# Revit family: CRTW1X4
name_source: partatom
category: Lighting Fixtures
units: mm (PartAtom-declared; Revit-internal decimal feet)

## family parameters
Always vertical = Yes
Cut with Voids When Loaded = No
Host = Ceiling
Light Source = Yes
Maintain Annotation Orientation = No
OmniClass Number = 23.80.70.11
OmniClass Title = Luminaries for Internal Lighting
Part Type = Normal
Room Calculation Point = No
Round Connector Dimension = Use Diameter
Shared = No

## types (5) — shared parameters
Color Filter = 16777215
Default Elevation = 0' - 0"
Description = LED Recessed Cleanroom Top Access Walkable with Overlapping Door Frame
Dimming Lamp Color Temperature Shift = <None>
Emit Shape Visible in Rendering = No
Emit from Rectangle Length = 1' - 3 3/32"
Emit from Rectangle Width = 4' - 3 3/32"
Housing Finish = <By Category>
Lamp = LED
Length = 4' - 3 3/32"
Lens Finish = <By Category>
Manufacturer = Certolux
Model = CRTW
Tilt Angle = 90.00°
URL = https://www.viscor.com
Voltage = 120 V
Width = 1' - 3 3/32"

## per-type parameters (varying)
| type | Apparent Load | Lamp Wattage | Photometric Web File |
| CRTAo1X4-LED840K035LUNV-DSA | 28 VA | 28 VA | CRTAO-1X4-LED840K035LUNV-DSA.ies |
| CRTAo1X4-LED840K055LUNV-DSA | 41 VA | 41 VA | CRTAO-1X4-LED840K055LUNV-DSA.ies |
| CRTAo1X4-LED840K070LUNV-DSA | 52 VA | 52 VA | CRTAO-1X4-LED840K070LUNV-DSA.ies |
| CRTAo1X4-LED840K100LUNV-DSA | 75 VA | 75 VA | CRTAO-1X4-LED840K100LUNV-DSA.ies |
| CRTAo1X4-LED840K120LUNV-DSA | 90 VA | 90 VA | CRTAO-1X4-LED840K120LUNV-DSA.ies |

## geometry (parser evidence)
native form markers: Sweep x3
no freeform markers — native parametric forms only
